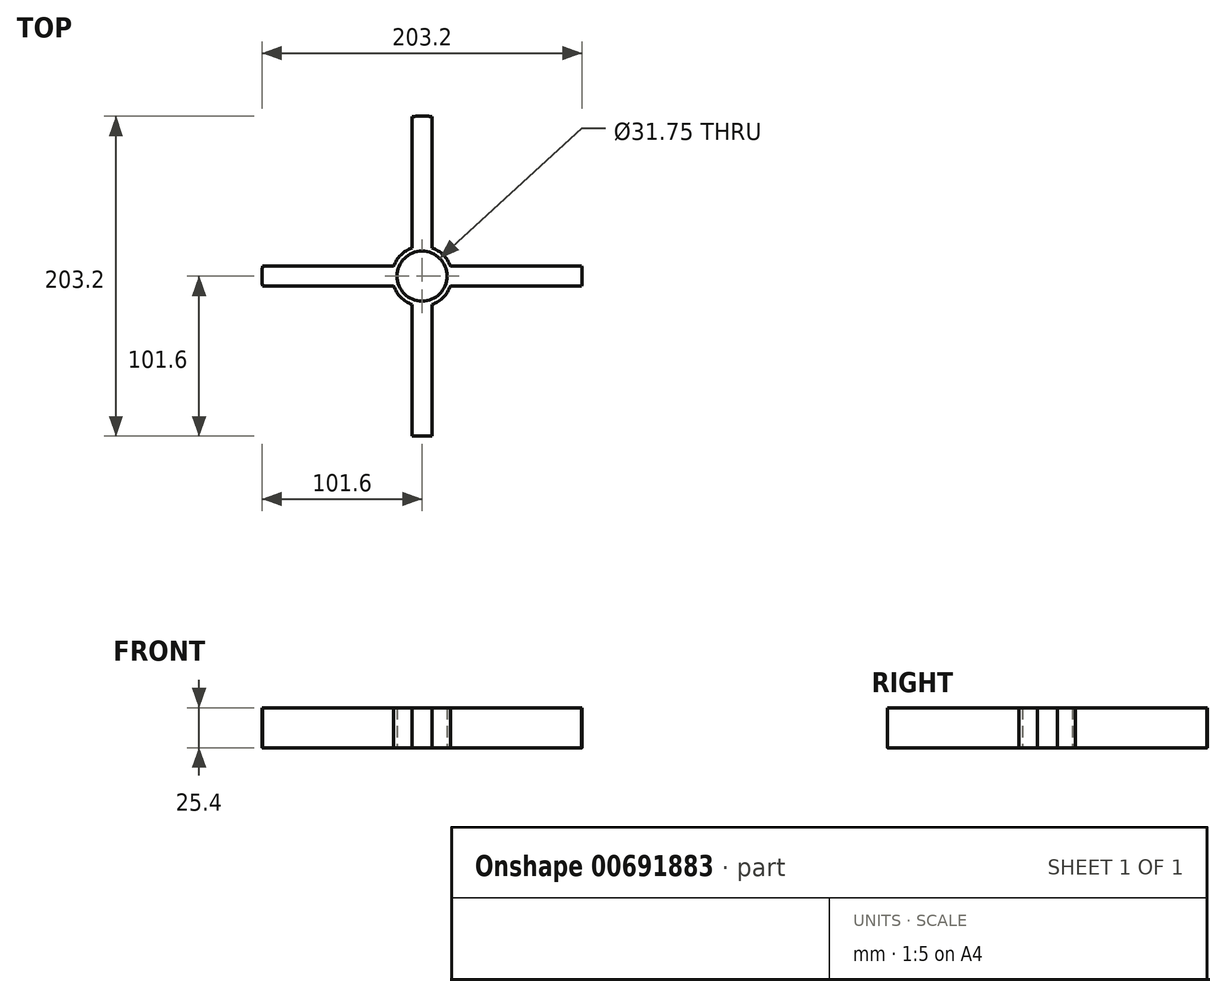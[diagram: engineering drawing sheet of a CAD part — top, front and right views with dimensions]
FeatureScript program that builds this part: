
annotation { "Feature Type Name" : "Feature", "Feature Type Description" : "" }
export const myFeature = defineFeature(function(context is Context, id is Id, definition is map)
    precondition{}
    {
        {
            var Q0;
            Q0=qCreatedBy(makeId("Top.planeOp"),FACE);
            var sketch = newSketch(context, id + "F0", { "sketchPlane" : qUnion([Q0])});
            skArc(sketch, "E0", {"start": v(-15.88, 0) * mm, "mid": v(14.67, -6.08) * mm, "end": v(-11.23, 11.23) * mm, "construction": true});
            skArc(sketch, "E1", {"start": v(-19.05, 0) * mm, "mid": v(17.6, -7.3) * mm, "end": v(-13.47, 13.47) * mm, "construction": true});
            skLineSegment(sketch, "E2", {"start": v(0, 0) * mm, "end": v(0, 19.05) * mm, "construction": true});
            skLineSegment(sketch, "E3", {"start": v(19.05, 0) * mm, "end": v(0, 0) * mm, "construction": true});
            skLineSegment(sketch, "E4", {"start": v(-19.05, 0) * mm, "end": v(0, 0) * mm, "construction": true});
            skLineSegment(sketch, "E5", {"start": v(0, 0) * mm, "end": v(0, -19.05) * mm, "construction": true});
            skLineSegment(sketch, "E6.left", {"start": v(0, 15.88) * mm, "end": v(0, 101.6) * mm});
            skLineSegment(sketch, "E6.right", {"start": v(-6.35, 17.96) * mm, "end": v(-6.35, 101.4) * mm});
            skArc(sketch, "E7", {"start": v(-13.47, 13.47) * mm, "mid": v(-10.16, 16.11) * mm, "end": v(-6.35, 17.96) * mm});
            skArc(sketch, "E8", {"start": v(-11.23, 11.23) * mm, "mid": v(-6.08, 14.67) * mm, "end": v(0, 15.88) * mm});
            skLineSegment(sketch, "E9", {"start": v(0, 15.88) * mm, "end": v(-15.88, 0) * mm, "construction": true});
            skLineSegment(sketch, "E10", {"start": v(-7.94, 7.94) * mm, "end": v(0, 0) * mm, "construction": true});
            skLineSegment(sketch, "E11", {"start": v(-7.94, 7.94) * mm, "end": v(-13.47, 13.47) * mm, "construction": true});
            skLineSegment(sketch, "E12", {"start": v(-11.23, 11.23) * mm, "end": v(-13.47, 13.47) * mm});
            skArc(sketch, "E13", {"start": v(0, 101.6) * mm, "mid": v(-3.18, 101.55) * mm, "end": v(-6.35, 101.4) * mm});
            skSolve(sketch);
        }
        {
            var Q0;
            Q0=makeQuery(id+"F0.imprint","IMPRINT",FACE,{"disambiguationData":[TD([[makeQuery(id+"F0.imprint","IMPRINT",EDGE,{"derivedFrom":sQuery(id+"F0.wireOp",EDGE,"E6.left")}),1.0]])]});
            var Q1;
            Q1=sQuery(id+"F0.wireOp",EDGE,"E6.right");
            var Q2;
            Q2=sQuery(id+"F0.wireOp",EDGE,"E13");
            var Q3;
            Q3=sQuery(id+"F0.wireOp",EDGE,"E6.left");
            var Q4;
            Q4=sQuery(id+"F0.wireOp",EDGE,"E8");
            var Q5;
            Q5=sQuery(id+"F0.wireOp",EDGE,"E12");
            var Q6;
            Q6=sQuery(id+"F0.wireOp",EDGE,"E7");
            extrude(context, id + "F1", {"entities" : qUnion([Q0]), "surfaceEntities" : qUnion([Q1, Q2, Q3, Q4, Q5, Q6]), "depth" : 25.4 * mm, "offsetDistance" : 25.4 * mm});
        }
        {
            var Q0;
            Q0=sQuery(id+"F0.wireOp",EDGE,"E10");
            cPlane(context, id + "F2", {"entities" : qUnion([Q0]), "cplaneType" : CPlaneType.LINE_ANGLE, "offset" : 25.4 * mm, "angle" : 90 * degree, "width" : 152.4 * mm, "height" : 152.4 * mm});
        }
        {
            var Q0;
            Q0=makeQuery(id+"F1.opExtrude","SWEPT_BODY",BODY,{"disambiguationData":[OSD([sQuery(id+"F0.wireOp",EDGE,"E6.top"),sQuery(id+"F0.wireOp",EDGE,"E6.left"),sQuery(id+"F0.wireOp",EDGE,"E6.right"),sQuery(id+"F0.wireOp",EDGE,"E7"),sQuery(id+"F0.wireOp",EDGE,"E8"),sQuery(id+"F0.wireOp",EDGE,"E12")])]});
            var Q1;
            Q1=qCreatedBy(id+"F2.planeOp",FACE);
            mirror(context, id + "F3", {"operationType" : NewBodyOperationType.ADD, "entities" : qUnion([Q0]), "mirrorPlane" : qUnion([Q1])});
        }
        {
            var Q0;
            Q0=makeQuery(id+"F1.opExtrude","SWEPT_BODY",BODY,{"disambiguationData":[OSD([sQuery(id+"F0.wireOp",EDGE,"E6.top"),sQuery(id+"F0.wireOp",EDGE,"E6.left"),sQuery(id+"F0.wireOp",EDGE,"E6.right"),sQuery(id+"F0.wireOp",EDGE,"E7"),sQuery(id+"F0.wireOp",EDGE,"E8"),sQuery(id+"F0.wireOp",EDGE,"E12")])]});
            var Q1;
            Q1=qCreatedBy(makeId("Front.planeOp"),FACE);
            mirror(context, id + "F4", {"operationType" : NewBodyOperationType.ADD, "entities" : qUnion([Q0]), "mirrorPlane" : qUnion([Q1])});
        }
        {
            var Q0;
            Q0=makeQuery(id+"F1.opExtrude","SWEPT_BODY",BODY,{"disambiguationData":[OSD([sQuery(id+"F0.wireOp",EDGE,"E6.top"),sQuery(id+"F0.wireOp",EDGE,"E6.left"),sQuery(id+"F0.wireOp",EDGE,"E6.right"),sQuery(id+"F0.wireOp",EDGE,"E7"),sQuery(id+"F0.wireOp",EDGE,"E8"),sQuery(id+"F0.wireOp",EDGE,"E12")])]});
            var Q1;
            Q1=qCreatedBy(makeId("Right.planeOp"),FACE);
            mirror(context, id + "F5", {"operationType" : NewBodyOperationType.ADD, "entities" : qUnion([Q0]), "mirrorPlane" : qUnion([Q1])});
        }
    });
